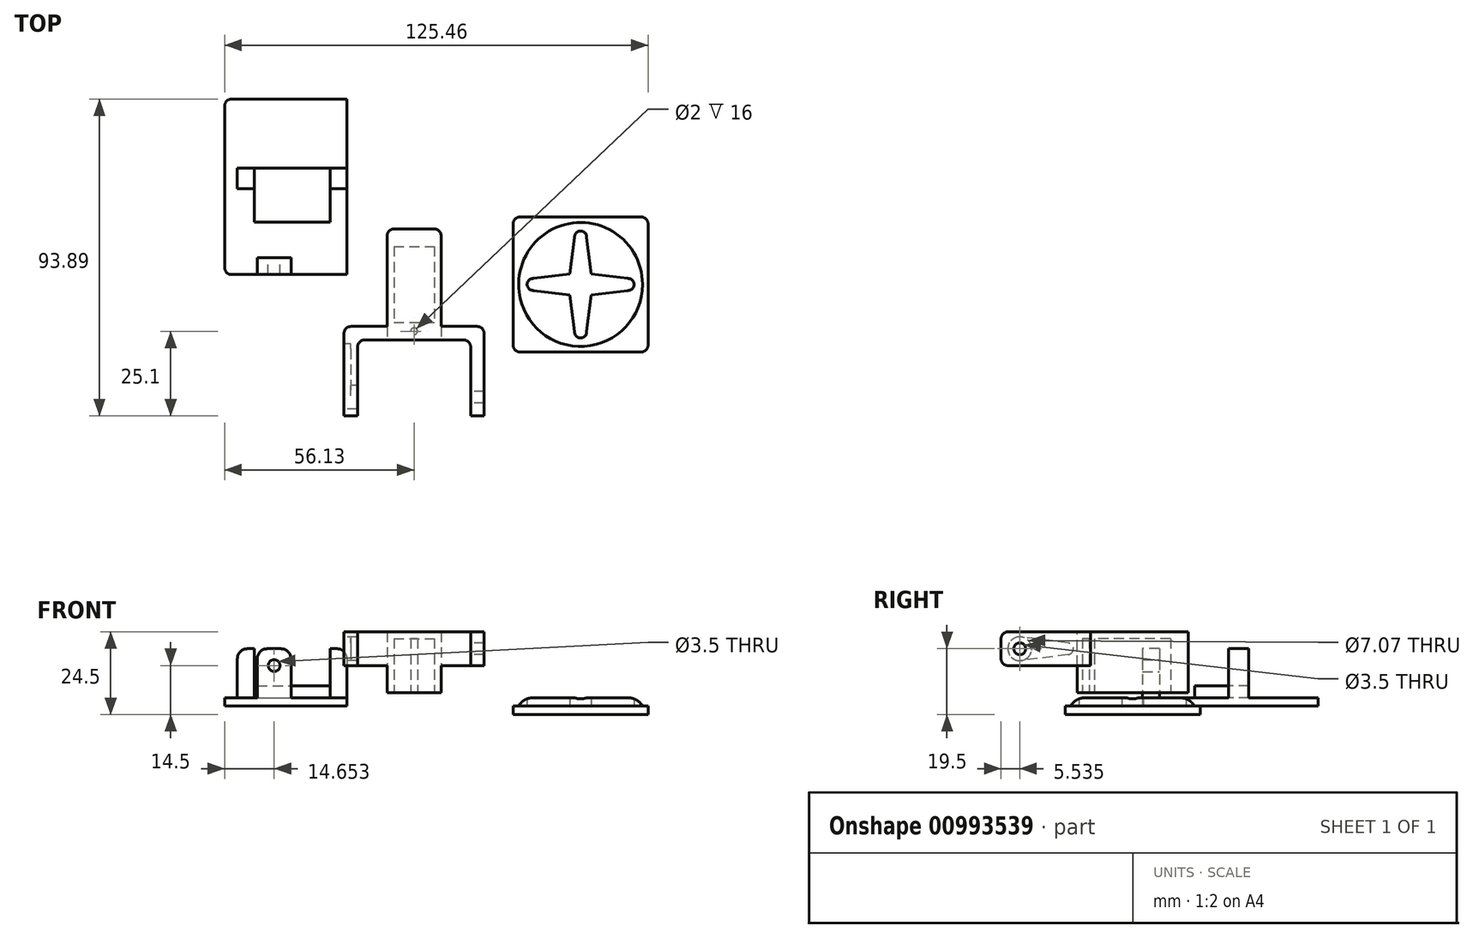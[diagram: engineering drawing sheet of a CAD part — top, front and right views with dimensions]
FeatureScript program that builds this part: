
annotation { "Feature Type Name" : "Feature", "Feature Type Description" : "" }
export const myFeature = defineFeature(function(context is Context, id is Id, definition is map)
    precondition{}
    {
        {
            var Q0;
            Q0=qCreatedBy(makeId("Top.planeOp"),FACE);
            var sketch = newSketch(context, id + "F0", { "sketchPlane" : qUnion([Q0])});
            skLineSegment(sketch, "E0.bottom", {"start": v(-6, 11.25) * mm, "end": v(6, 11.25) * mm});
            skLineSegment(sketch, "E0.top", {"start": v(-6, -11.25) * mm, "end": v(6, -11.25) * mm});
            skLineSegment(sketch, "E0.left", {"start": v(-6, 11.25) * mm, "end": v(-6, -11.25) * mm});
            skLineSegment(sketch, "E0.right", {"start": v(6, 11.25) * mm, "end": v(6, -11.25) * mm});
            skLineSegment(sketch, "E1.bottom", {"start": v(-8, 16.45) * mm, "end": v(8, 16.45) * mm});
            skLineSegment(sketch, "E1.top", {"start": v(-8, -16.45) * mm, "end": v(8, -16.45) * mm});
            skLineSegment(sketch, "E1.left", {"start": v(-8, 16.45) * mm, "end": v(-8, -16.45) * mm});
            skLineSegment(sketch, "E1.right", {"start": v(8, 16.45) * mm, "end": v(8, -16.45) * mm});
            skCircle(sketch, "E2", {"center": v(0, 13.85) * mm, "radius": 1 * mm});
            skLineSegment(sketch, "E3", {"start": v(-8, 0) * mm, "end": v(8, 0) * mm, "construction": true});
            skPoint(sketch, "E3.endSnap0", {"position": v(6, 0) * mm});
            skLineSegment(sketch, "E4", {"start": v(0, 13.85) * mm, "end": v(0, 13.85) * mm});
            skLineSegment(sketch, "E5", {"start": v(0, 0) * mm, "end": v(0, 13.85) * mm, "construction": true});
            skCircle(sketch, "E6.MirrorC", {"center": v(0, -13.85) * mm, "radius": 1 * mm});
            skLineSegment(sketch, "E7", {"start": v(0, -16.45) * mm, "end": v(0, -13.85) * mm, "construction": true});
            skLineSegment(sketch, "E8", {"start": v(0, -11.25) * mm, "end": v(0, -13.85) * mm, "construction": true});
            skSolve(sketch);
        }
        {
            var Q0;
            Q0=makeQuery(id+"F0.imprint","IMPRINT",FACE,{"disambiguationData":[TD([[makeQuery(id+"F0.imprint","IMPRINT",EDGE,{"derivedFrom":sQuery(id+"F0.wireOp",EDGE,"E2")}),1.0]])]});
            var Q1;
            Q1=makeQuery(id+"F0.imprint","IMPRINT",FACE,{"disambiguationData":[TD([[makeQuery(id+"F0.imprint","IMPRINT",EDGE,{"derivedFrom":sQuery(id+"F0.wireOp",EDGE,"E2")}),1.0]])]});
            var Q2;
            Q2=makeQuery(id+"F0.imprint","IMPRINT",FACE,{"disambiguationData":[TD([[makeQuery(id+"F0.imprint","IMPRINT",EDGE,{"derivedFrom":sQuery(id+"F0.wireOp",EDGE,"E6.MirrorC")}),-1.0]])]});
            var Q3;
            Q3=makeQuery(id+"F0.imprint","IMPRINT",FACE,{"disambiguationData":[TD([[makeQuery(id+"F0.imprint","IMPRINT",EDGE,{"derivedFrom":sQuery(id+"F0.wireOp",EDGE,"E0.bottom")}),1.0]])]});
            var Q4;
            Q4=makeQuery(id+"F0.imprint","IMPRINT",FACE,{"disambiguationData":[TD([[makeQuery(id+"F0.imprint","IMPRINT",EDGE,{"derivedFrom":sQuery(id+"F0.wireOp",EDGE,"E6.MirrorC")}),-1.0]])]});
            extrude(context, id + "F1", {"entities" : qUnion([Q0, Q1, Q2, Q3, Q4]), "depth" : 20 * mm, "offsetDistance" : 25 * mm});
        }
        {
            var Q0;
            Q0=makeQuery(id+"F0.imprint","IMPRINT",FACE,{"disambiguationData":[TD([[makeQuery(id+"F0.imprint","IMPRINT",EDGE,{"derivedFrom":sQuery(id+"F0.wireOp",EDGE,"E2")}),1.0]])]});
            var Q1;
            Q1=makeQuery(id+"F0.imprint","IMPRINT",FACE,{"disambiguationData":[TD([[makeQuery(id+"F0.imprint","IMPRINT",EDGE,{"derivedFrom":sQuery(id+"F0.wireOp",EDGE,"E2")}),1.0]])]});
            var Q2;
            Q2=makeQuery(id+"F0.imprint","IMPRINT",FACE,{"disambiguationData":[TD([[makeQuery(id+"F0.imprint","IMPRINT",EDGE,{"derivedFrom":sQuery(id+"F0.wireOp",EDGE,"E6.MirrorC")}),-1.0]])]});
            var Q3;
            Q3=makeQuery(id+"F0.imprint","IMPRINT",FACE,{"disambiguationData":[TD([[makeQuery(id+"F0.imprint","IMPRINT",EDGE,{"derivedFrom":sQuery(id+"F0.wireOp",EDGE,"E6.MirrorC")}),-1.0]])]});
            extrude(context, id + "F2", {"entities" : qUnion([Q0, Q1, Q2, Q3]), "operationType" : NewBodyOperationType.REMOVE, "depth" : 4 * mm, "offsetDistance" : 25 * mm});
        }
        {
            var Q0;
            Q0=makeQuery(id+"F1.opExtrude","CAP_FACE",FACE,{"disambiguationData":[OSD([sQuery(id+"F0.wireOp",EDGE,"E0.bottom"),sQuery(id+"F0.wireOp",EDGE,"E0.top"),sQuery(id+"F0.wireOp",EDGE,"E0.left"),sQuery(id+"F0.wireOp",EDGE,"E0.right"),sQuery(id+"F0.wireOp",EDGE,"E1.bottom"),sQuery(id+"F0.wireOp",EDGE,"E1.top"),sQuery(id+"F0.wireOp",EDGE,"E1.left"),sQuery(id+"F0.wireOp",EDGE,"E1.right")])],"isStart":false});
            var sketch = newSketch(context, id + "F3", { "sketchPlane" : qUnion([Q0])});
            skLineSegment(sketch, "E9.bottom", {"start": v(-8, 16.45) * mm, "end": v(8, 16.45) * mm});
            skLineSegment(sketch, "E9.top", {"start": v(-8, -16.45) * mm, "end": v(8, -16.45) * mm});
            skLineSegment(sketch, "E9.left", {"start": v(-8, 16.45) * mm, "end": v(-8, -16.45) * mm});
            skLineSegment(sketch, "E9.right", {"start": v(8, 16.45) * mm, "end": v(8, -16.45) * mm});
            skSolve(sketch);
        }
        {
            var Q0;
            Q0 = qSketchRegion(id + "F3", true);
            extrude(context, id + "F4", {"entities" : qUnion([Q0]), "operationType" : NewBodyOperationType.ADD, "depth" : 2 * mm, "offsetDistance" : 25 * mm});
        }
        {
            var Q0;
            Q0=makeQuery(id+"F4.opExtrude","CAP_FACE",FACE,{"disambiguationData":[OSD([sQuery(id+"F3.wireOp",EDGE,"E9.bottom"),sQuery(id+"F3.wireOp",EDGE,"E9.top"),sQuery(id+"F3.wireOp",EDGE,"E9.left"),sQuery(id+"F3.wireOp",EDGE,"E9.right")])],"isStart":false});
            var sketch = newSketch(context, id + "F5", { "sketchPlane" : qUnion([Q0])});
            skLineSegment(sketch, "E10", {"start": v(-16.75, -16.45) * mm, "end": v(16.75, -16.45) * mm});
            skLineSegment(sketch, "E11", {"start": v(-16.75, -16.45) * mm, "end": v(-16.75, -38.95) * mm});
            skLineSegment(sketch, "E12", {"start": v(-16.75, -38.95) * mm, "end": v(-20.75, -38.95) * mm});
            skLineSegment(sketch, "E13", {"start": v(-20.75, -38.95) * mm, "end": v(-20.75, -12.45) * mm});
            skLineSegment(sketch, "E14", {"start": v(-20.75, -12.45) * mm, "end": v(-8, -12.45) * mm});
            skLineSegment(sketch, "E15", {"start": v(16.75, -16.45) * mm, "end": v(16.75, -38.95) * mm});
            skLineSegment(sketch, "E16", {"start": v(16.75, -38.95) * mm, "end": v(20.75, -38.95) * mm});
            skLineSegment(sketch, "E17", {"start": v(20.75, -38.95) * mm, "end": v(20.75, -12.45) * mm});
            skLineSegment(sketch, "E18", {"start": v(20.75, -12.45) * mm, "end": v(8, -12.45) * mm});
            skLineSegment(sketch, "E19", {"start": v(16.75, -16.45) * mm, "end": v(20.75, -12.45) * mm, "construction": true});
            skSolve(sketch);
        }
        {
            var Q0;
            Q0 = qSketchRegion(id + "F5", true);
            var Q1;
            {var subQ0=sQuery(id+"F5.wireOp",EDGE,"E15");Q1=makeQuery(id+"F5.imprint","IMPRINT",FACE,{"disambiguationData":[TD([[makeQuery(id+"F5.imprint","IMPRINT",EDGE,{"derivedFrom":subQ0}),1.0]])]});}
            var Q2;
            {var subQ0=sQuery(id+"F5.wireOp",EDGE,"E11");Q2=makeQuery(id+"F5.imprint","IMPRINT",FACE,{"disambiguationData":[TD([[makeQuery(id+"F5.imprint","IMPRINT",EDGE,{"derivedFrom":subQ0}),-1.0]])]});}
            extrude(context, id + "F6", {"entities" : qUnion([Q0, Q1, Q2]), "operationType" : NewBodyOperationType.ADD, "oppositeDirection" : true, "depth" : 10 * mm, "offsetDistance" : 25 * mm});
        }
        {
            var Q0;
            Q0=makeQuery(id+"F6.opExtrude","SWEPT_EDGE",EDGE,{"disambiguationData":[OSD([sQuery(id+"F5.wireOp",EDGE,"E13"),sQuery(id+"F5.wireOp",EDGE,"E14")])]});
            var Q1;
            Q1=makeQuery(id+"F6.opExtrude","SWEPT_EDGE",EDGE,{"disambiguationData":[OSD([sQuery(id+"F5.wireOp",EDGE,"E17"),sQuery(id+"F5.wireOp",EDGE,"E18")])]});
            var Q2;
            Q2=makeQuery(id+"F6.opExtrude","CAP_EDGE",EDGE,{"disambiguationData":[OSD([sQuery(id+"F5.wireOp",EDGE,"E16")])],"isStart":true});
            var Q3;
            Q3=makeQuery(id+"F6.opExtrude","CAP_EDGE",EDGE,{"disambiguationData":[OSD([sQuery(id+"F5.wireOp",EDGE,"E16")])],"isStart":false});
            var Q4;
            Q4=makeQuery(id+"F6.opExtrude","CAP_EDGE",EDGE,{"disambiguationData":[OSD([sQuery(id+"F5.wireOp",EDGE,"E12")])],"isStart":true});
            var Q5;
            Q5=makeQuery(id+"F6.opExtrude","CAP_EDGE",EDGE,{"disambiguationData":[OSD([sQuery(id+"F5.wireOp",EDGE,"E12")])],"isStart":false});
            var Q6;
            Q6=makeQuery(id+"F6.opExtrude","SWEPT_EDGE",EDGE,{"disambiguationData":[OSD([sQuery(id+"F5.wireOp",EDGE,"E10"),sQuery(id+"F5.wireOp",EDGE,"E11")])]});
            var Q7;
            Q7=makeQuery(id+"F6.opExtrude","SWEPT_EDGE",EDGE,{"disambiguationData":[OSD([sQuery(id+"F5.wireOp",EDGE,"E10"),sQuery(id+"F5.wireOp",EDGE,"E15")])]});
            var Q8;
            Q8=makeQuery(id+"F4.boolean.opBoolean","MERGE",EDGE,{"derivedFrom":[makeQuery(id+"F1.opExtrude","SWEPT_EDGE",EDGE,{"disambiguationData":[OSD([sQuery(id+"F0.wireOp",EDGE,"E1.bottom"),sQuery(id+"F0.wireOp",EDGE,"E1.left")])]}),makeQuery(id+"F4.opExtrude","SWEPT_EDGE",EDGE,{"disambiguationData":[OSD([sQuery(id+"F3.wireOp",EDGE,"E9.bottom"),sQuery(id+"F3.wireOp",EDGE,"E9.left")])]})]});
            var Q9;
            Q9=makeQuery(id+"F4.boolean.opBoolean","MERGE",EDGE,{"derivedFrom":[makeQuery(id+"F1.opExtrude","SWEPT_EDGE",EDGE,{"disambiguationData":[OSD([sQuery(id+"F0.wireOp",EDGE,"E1.bottom"),sQuery(id+"F0.wireOp",EDGE,"E1.right")])]}),makeQuery(id+"F4.opExtrude","SWEPT_EDGE",EDGE,{"disambiguationData":[OSD([sQuery(id+"F3.wireOp",EDGE,"E9.bottom"),sQuery(id+"F3.wireOp",EDGE,"E9.right")])]})]});
            fillet(context, id + "F7", {"entities" : qUnion([Q0, Q1, Q2, Q3, Q4, Q5, Q6, Q7, Q8, Q9]), "radius" : 2 * mm, "tangentPropagation" : true, "allowEdgeOverflow" : false});
        }
        {
            var Q0;
            Q0=makeQuery(id+"F6.opExtrude","SWEPT_FACE",FACE,{"disambiguationData":[OSD([sQuery(id+"F5.wireOp",EDGE,"E13")])]});
            var sketch = newSketch(context, id + "F8", { "sketchPlane" : qUnion([Q0])});
            skCircle(sketch, "E20", {"center": v(33.41, 17) * mm, "radius": 3.54 * mm});
            skCircle(sketch, "E21", {"center": v(19.33, 17) * mm, "radius": 1.78 * mm});
            skLineSegment(sketch, "E22", {"start": v(14.45, 17) * mm, "end": v(38.95, 17) * mm, "construction": true});
            skLineSegment(sketch, "E23", {"start": v(19.1, 18.77) * mm, "end": v(32.97, 20.5) * mm});
            skLineSegment(sketch, "E24.MirrorCS", {"start": v(19.1, 15.23) * mm, "end": v(32.97, 13.5) * mm});
            skPoint(sketch, "E25", {"position": v(17.55, 17) * mm});
            skPoint(sketch, "E26", {"position": v(36.95, 17) * mm});
            skSolve(sketch);
        }
        {
            var Q0;
            {var subQ0=sQuery(id+"F8.wireOp",EDGE,"E21");var subQ1=makeQuery(id+"F8.imprint","INTERSECT",VERTEX,{"derivedFrom":[subQ0,sQuery(id+"F8.wireOp",EDGE,"E23")]});Q0=makeQuery(id+"F8.imprint","IMPRINT",FACE,{"disambiguationData":[TD([[makeQuery(id+"F8.imprint","IMPRINT",EDGE,{"disambiguationData":[TD([[subQ1,-1.0]])],"derivedFrom":subQ0}),1.0]])]});}
            var Q1;
            {var subQ0=sQuery(id+"F8.wireOp",EDGE,"E23");Q1=makeQuery(id+"F8.imprint","IMPRINT",FACE,{"disambiguationData":[TD([[makeQuery(id+"F8.imprint","IMPRINT",EDGE,{"derivedFrom":subQ0}),-1.0]])]});}
            var Q2;
            {var subQ0=sQuery(id+"F8.wireOp",EDGE,"E20");var subQ1=makeQuery(id+"F8.imprint","INTERSECT",VERTEX,{"derivedFrom":[subQ0,sQuery(id+"F8.wireOp",EDGE,"E23")]});Q2=makeQuery(id+"F8.imprint","IMPRINT",FACE,{"disambiguationData":[TD([[makeQuery(id+"F8.imprint","IMPRINT",EDGE,{"disambiguationData":[TD([[subQ1,-1.0]])],"derivedFrom":subQ0}),1.0]])]});}
            extrude(context, id + "F9", {"entities" : qUnion([Q0, Q1, Q2]), "operationType" : NewBodyOperationType.REMOVE, "oppositeDirection" : true, "depth" : 2 * mm, "offsetDistance" : 25 * mm});
        }
        {
            var Q0;
            {var subQ0=sQuery(id+"F8.wireOp",EDGE,"E20");var subQ1=makeQuery(id+"F8.imprint","INTERSECT",VERTEX,{"derivedFrom":[subQ0,sQuery(id+"F8.wireOp",EDGE,"E23")]});Q0=makeQuery(id+"F8.imprint","IMPRINT",FACE,{"disambiguationData":[TD([[makeQuery(id+"F8.imprint","IMPRINT",EDGE,{"disambiguationData":[TD([[subQ1,-1.0]])],"derivedFrom":subQ0}),1.0]])]});}
            var Q1;
            Q1=makeQuery(id+"F6.opExtrude","SWEPT_FACE",FACE,{"disambiguationData":[OSD([sQuery(id+"F5.wireOp",EDGE,"E11")])]});
            extrude(context, id + "F10", {"entities" : qUnion([Q0]), "operationType" : NewBodyOperationType.REMOVE, "endBound" : BoundingType.UP_TO_SURFACE, "oppositeDirection" : true, "depth" : 25 * mm, "endBoundEntityFace" : qUnion([Q1]), "offsetDistance" : 25 * mm});
        }
        {
            var Q0;
            Q0=qCreatedBy(makeId("Top.planeOp"),FACE);
            var sketch = newSketch(context, id + "F11", { "sketchPlane" : qUnion([Q0])});
            skLineSegment(sketch, "E27.bottom", {"start": v(-56.13, 42.94) * mm, "end": v(-16.13, 42.94) * mm});
            skLineSegment(sketch, "E27.top", {"start": v(-56.13, 2.94) * mm, "end": v(-16.13, 2.94) * mm});
            skLineSegment(sketch, "E27.left", {"start": v(-56.13, 42.94) * mm, "end": v(-56.13, 2.94) * mm});
            skLineSegment(sketch, "E27.right", {"start": v(-16.13, 42.94) * mm, "end": v(-16.13, 2.94) * mm});
            skSolve(sketch);
        }
        {
            var Q0;
            Q0=makeQuery(id+"F11.imprint","IMPRINT",FACE,{"disambiguationData":[TD([[makeQuery(id+"F11.imprint","IMPRINT",EDGE,{"derivedFrom":sQuery(id+"F11.wireOp",EDGE,"E27.bottom")}),-1.0]])]});
            extrude(context, id + "F12", {"entities" : qUnion([Q0]), "depth" : 2.5 * mm, "offsetDistance" : 25 * mm});
        }
        {
            var Q0;
            Q0=makeQuery(id+"F12.opExtrude","CAP_FACE",FACE,{"disambiguationData":[OSD([sQuery(id+"F11.wireOp",EDGE,"E27.bottom"),sQuery(id+"F11.wireOp",EDGE,"E27.top"),sQuery(id+"F11.wireOp",EDGE,"E27.left"),sQuery(id+"F11.wireOp",EDGE,"E27.right")])],"isStart":false});
            var sketch = newSketch(context, id + "F13", { "sketchPlane" : qUnion([Q0])});
            skLineSegment(sketch, "E28.bottom", {"start": v(-47.38, 34.44) * mm, "end": v(-24.88, 34.44) * mm});
            skLineSegment(sketch, "E28.top", {"start": v(-47.38, 18.44) * mm, "end": v(-24.88, 18.44) * mm});
            skLineSegment(sketch, "E28.left", {"start": v(-47.38, 34.44) * mm, "end": v(-47.38, 18.44) * mm});
            skLineSegment(sketch, "E28.right", {"start": v(-24.88, 34.44) * mm, "end": v(-24.88, 18.44) * mm});
            skPoint(sketch, "E29", {"position": v(-36.13, 26.44) * mm});
            skLineSegment(sketch, "E30.bottom", {"start": v(-24.88, 34.44) * mm, "end": v(-19.88, 34.44) * mm});
            skLineSegment(sketch, "E30.top", {"start": v(-24.88, 28.44) * mm, "end": v(-19.88, 28.44) * mm});
            skLineSegment(sketch, "E30.left", {"start": v(-24.88, 34.44) * mm, "end": v(-24.88, 28.44) * mm});
            skLineSegment(sketch, "E30.right", {"start": v(-19.88, 34.44) * mm, "end": v(-19.88, 28.44) * mm});
            skLineSegment(sketch, "E31.bottom", {"start": v(-47.38, 34.44) * mm, "end": v(-52.38, 34.44) * mm});
            skLineSegment(sketch, "E31.top", {"start": v(-47.38, 28.44) * mm, "end": v(-52.38, 28.44) * mm});
            skLineSegment(sketch, "E31.left", {"start": v(-47.38, 34.44) * mm, "end": v(-47.38, 28.44) * mm});
            skLineSegment(sketch, "E31.right", {"start": v(-52.38, 34.44) * mm, "end": v(-52.38, 28.44) * mm});
            skLineSegment(sketch, "E32", {"start": v(-41.48, 2.94) * mm, "end": v(-41.48, 42.94) * mm, "construction": true});
            skLineSegment(sketch, "E33.bottom", {"start": v(-46.48, 7.94) * mm, "end": v(-36.48, 7.94) * mm});
            skLineSegment(sketch, "E33.top", {"start": v(-46.48, 2.94) * mm, "end": v(-36.48, 2.94) * mm});
            skLineSegment(sketch, "E33.left", {"start": v(-46.48, 7.94) * mm, "end": v(-46.48, 2.94) * mm});
            skLineSegment(sketch, "E33.right", {"start": v(-36.48, 7.94) * mm, "end": v(-36.48, 2.94) * mm});
            skSolve(sketch);
        }
        {
            var Q0;
            {var subQ0=sQuery(id+"F13.wireOp",EDGE,"E31.bottom");Q0=makeQuery(id+"F13.imprint","IMPRINT",FACE,{"disambiguationData":[TD([[makeQuery(id+"F13.imprint","IMPRINT",EDGE,{"derivedFrom":subQ0}),1.0]])]});}
            var Q1;
            {var subQ0=sQuery(id+"F13.wireOp",EDGE,"E30.bottom");Q1=makeQuery(id+"F13.imprint","IMPRINT",FACE,{"disambiguationData":[TD([[makeQuery(id+"F13.imprint","IMPRINT",EDGE,{"derivedFrom":subQ0}),-1.0]])]});}
            var Q2;
            Q2=makeQuery(id+"F13.imprint","IMPRINT",FACE,{"disambiguationData":[TD([[makeQuery(id+"F13.imprint","IMPRINT",EDGE,{"derivedFrom":sQuery(id+"F13.wireOp",EDGE,"E33.bottom")}),-1.0]])]});
            extrude(context, id + "F14", {"entities" : qUnion([Q0, Q1, Q2]), "operationType" : NewBodyOperationType.ADD, "depth" : 14.5 * mm, "offsetDistance" : 25 * mm});
        }
        {
            var Q0;
            {var subQ1=sQuery(id+"F13.wireOp",EDGE,"E28.bottom");Q0=makeQuery(id+"F13.imprint","IMPRINT",FACE,{"disambiguationData":[TD([[makeQuery(id+"F13.imprint","IMPRINT",EDGE,{"derivedFrom":subQ1}),-1.0]])]});}
            extrude(context, id + "F15", {"entities" : qUnion([Q0]), "operationType" : NewBodyOperationType.ADD, "depth" : 3.5 * mm, "offsetDistance" : 25 * mm});
        }
        {
            var Q0;
            Q0=makeQuery(id+"F14.opExtrude","CAP_EDGE",EDGE,{"disambiguationData":[OSD([sQuery(id+"F13.wireOp",EDGE,"E31.right")])],"isStart":false});
            var Q1;
            Q1=makeQuery(id+"F14.opExtrude","CAP_EDGE",EDGE,{"disambiguationData":[OSD([sQuery(id+"F13.wireOp",EDGE,"E30.right")])],"isStart":false});
            var Q2;
            Q2=makeQuery(id+"F14.opExtrude","CAP_EDGE",EDGE,{"disambiguationData":[OSD([sQuery(id+"F13.wireOp",EDGE,"E33.left")])],"isStart":false});
            var Q3;
            Q3=makeQuery(id+"F14.opExtrude","CAP_EDGE",EDGE,{"disambiguationData":[OSD([sQuery(id+"F13.wireOp",EDGE,"E33.right")])],"isStart":false});
            fillet(context, id + "F16", {"entities" : qUnion([Q0, Q1, Q2, Q3]), "radius" : 3 * mm, "allowEdgeOverflow" : false});
        }
        {
            var Q0;
            Q0=makeQuery(id+"F12.opExtrude","SWEPT_FACE",FACE,{"disambiguationData":[OSD([sQuery(id+"F11.wireOp",EDGE,"E27.bottom")])]});
            extrude(context, id + "F17", {"entities" : qUnion([Q0]), "operationType" : NewBodyOperationType.ADD, "depth" : 12 * mm, "offsetDistance" : 25 * mm});
        }
        {
            var Q0;
            {var subQ0=sQuery(id+"F11.wireOp",EDGE,"E27.right");Q0=makeQuery(id+"F17.boolean.opBoolean","MERGE",FACE,{"derivedFrom":[makeQuery(id+"F12.opExtrude","SWEPT_FACE",FACE,{"disambiguationData":[OSD([subQ0])]}),makeQuery(id+"F17.opExtrude","SWEPT_FACE",FACE,{"disambiguationData":[OSD([sQuery(id+"F11.wireOp",EDGE,"E27.bottom"),subQ0])]})]});}
            var Q1;
            Q1=makeQuery(id+"F14.opExtrude","SWEPT_FACE",FACE,{"disambiguationData":[OSD([sQuery(id+"F13.wireOp",EDGE,"E30.right")])]});
            extrude(context, id + "F18", {"entities" : qUnion([Q0]), "operationType" : NewBodyOperationType.REMOVE, "endBound" : BoundingType.UP_TO_SURFACE, "oppositeDirection" : true, "depth" : 25 * mm, "endBoundEntityFace" : qUnion([Q1]), "offsetDistance" : 25 * mm});
        }
        {
            var Q0;
            Q0=makeQuery(id+"F6.opExtrude","SWEPT_FACE",FACE,{"disambiguationData":[OSD([sQuery(id+"F5.wireOp",EDGE,"E15")])]});
            var sketch = newSketch(context, id + "F19", { "sketchPlane" : qUnion([Q0])});
            skCircle(sketch, "E34", {"center": v(33.41, 17) * mm, "radius": 1.75 * mm});
            skSolve(sketch);
        }
        {
            var Q0;
            Q0=makeQuery(id+"F19.imprint","IMPRINT",FACE,{"disambiguationData":[TD([[makeQuery(id+"F19.imprint","IMPRINT",EDGE,{"derivedFrom":sQuery(id+"F19.wireOp",EDGE,"E34")}),1.0]])]});
            var Q1;
            Q1=makeQuery(id+"F6.opExtrude","SWEPT_FACE",FACE,{"disambiguationData":[OSD([sQuery(id+"F5.wireOp",EDGE,"E17")])]});
            extrude(context, id + "F20", {"entities" : qUnion([Q0]), "operationType" : NewBodyOperationType.REMOVE, "endBound" : BoundingType.UP_TO_SURFACE, "oppositeDirection" : true, "depth" : 25 * mm, "endBoundEntityFace" : qUnion([Q1]), "offsetDistance" : 25 * mm});
        }
        {
            var Q0;
            Q0=makeQuery(id+"F14.opExtrude","SWEPT_FACE",FACE,{"disambiguationData":[OSD([sQuery(id+"F13.wireOp",EDGE,"E33.bottom")])]});
            var sketch = newSketch(context, id + "F21", { "sketchPlane" : qUnion([Q0])});
            skCircle(sketch, "E35", {"center": v(41.48, 12) * mm, "radius": 1.75 * mm});
            skSolve(sketch);
        }
        {
            var Q0;
            Q0=makeQuery(id+"F21.imprint","IMPRINT",FACE,{"disambiguationData":[TD([[makeQuery(id+"F21.imprint","IMPRINT",EDGE,{"derivedFrom":sQuery(id+"F21.wireOp",EDGE,"E35")}),1.0]])]});
            var Q1;
            Q1=makeQuery(id+"F14.boolean.opBoolean","MERGE",FACE,{"derivedFrom":[makeQuery(id+"F12.opExtrude","SWEPT_FACE",FACE,{"disambiguationData":[OSD([sQuery(id+"F11.wireOp",EDGE,"E27.top")])]}),makeQuery(id+"F14.opExtrude","SWEPT_FACE",FACE,{"disambiguationData":[OSD([sQuery(id+"F13.wireOp",EDGE,"E33.top")])]})]});
            extrude(context, id + "F22", {"entities" : qUnion([Q0]), "operationType" : NewBodyOperationType.REMOVE, "endBound" : BoundingType.UP_TO_SURFACE, "oppositeDirection" : true, "depth" : 25 * mm, "endBoundEntityFace" : qUnion([Q1]), "offsetDistance" : 25 * mm});
        }
        {
            var Q0;
            Q0=qCreatedBy(makeId("Top.planeOp"),FACE);
            var sketch = newSketch(context, id + "F23", { "sketchPlane" : qUnion([Q0])});
            skLineSegment(sketch, "E36.bottom", {"start": v(29.33, -20) * mm, "end": v(69.33, -20) * mm});
            skLineSegment(sketch, "E36.top", {"start": v(29.33, 20) * mm, "end": v(69.33, 20) * mm});
            skLineSegment(sketch, "E36.left", {"start": v(29.33, -20) * mm, "end": v(29.33, 20) * mm});
            skLineSegment(sketch, "E36.right", {"start": v(69.33, -20) * mm, "end": v(69.33, 20) * mm});
            skCircle(sketch, "E37", {"center": v(49.33, 0) * mm, "radius": 3.54 * mm, "construction": true});
            skCircle(sketch, "E38", {"center": v(35.24, 0) * mm, "radius": 1.78 * mm});
            skPoint(sketch, "E39", {"position": v(33.46, 0) * mm});
            skPoint(sketch, "E40", {"position": v(52.86, 0) * mm});
            skPoint(sketch, "E41", {"position": v(49.33, 20) * mm});
            skPoint(sketch, "E42", {"position": v(29.33, 0) * mm});
            skLineSegment(sketch, "E43", {"start": v(35.02, 1.77) * mm, "end": v(48.89, 3.5) * mm});
            skLineSegment(sketch, "E44", {"start": v(35.02, -1.77) * mm, "end": v(48.89, -3.5) * mm});
            skLineSegment(sketch, "E45.1.0", {"start": v(47.56, -14.3) * mm, "end": v(45.82, -0.44) * mm});
            skCircle(sketch, "E45.1.1", {"center": v(49.33, -14.09) * mm, "radius": 1.78 * mm});
            skLineSegment(sketch, "E45.1.2", {"start": v(51.1, -14.3) * mm, "end": v(52.84, -0.44) * mm});
            skLineSegment(sketch, "E45.2.0", {"start": v(63.64, -1.77) * mm, "end": v(49.77, -3.5) * mm});
            skCircle(sketch, "E45.2.1", {"center": v(63.41, 0) * mm, "radius": 1.78 * mm});
            skLineSegment(sketch, "E45.2.2", {"start": v(63.64, 1.77) * mm, "end": v(49.77, 3.5) * mm});
            skLineSegment(sketch, "E45.3.0", {"start": v(51.1, 14.3) * mm, "end": v(52.84, 0.44) * mm});
            skCircle(sketch, "E45.3.1", {"center": v(49.33, 14.09) * mm, "radius": 1.78 * mm});
            skLineSegment(sketch, "E45.3.2", {"start": v(47.56, 14.3) * mm, "end": v(45.82, 0.44) * mm});
            skSolve(sketch);
        }
        {
            var Q0;
            Q0=makeQuery(id+"F23.imprint","IMPRINT",FACE,{"disambiguationData":[TD([[makeQuery(id+"F23.imprint","IMPRINT",EDGE,{"derivedFrom":sQuery(id+"F23.wireOp",EDGE,"E36.bottom")}),1.0]])]});
            var Q1;
            {var subQ15=sQuery(id+"F23.wireOp",EDGE,"E43");var subQ16=sQuery(id+"F23.wireOp",EDGE,"E38");var subQ17=makeQuery(id+"F23.imprint","INTERSECT",VERTEX,{"derivedFrom":[subQ16,subQ15]});Q1=makeQuery(id+"F23.imprint","IMPRINT",FACE,{"disambiguationData":[TD([[makeQuery(id+"F23.imprint","IMPRINT",EDGE,{"disambiguationData":[TD([[subQ17,1.0]])],"derivedFrom":subQ16}),-1.0]])]});}
            var Q2;
            {var subQ0=sQuery(id+"F23.wireOp",EDGE,"E45.3.1");var subQ1=makeQuery(id+"F23.imprint","INTERSECT",VERTEX,{"derivedFrom":[sQuery(id+"F23.wireOp",EDGE,"E45.3.0"),subQ0]});Q2=makeQuery(id+"F23.imprint","IMPRINT",FACE,{"disambiguationData":[TD([[makeQuery(id+"F23.imprint","IMPRINT",EDGE,{"disambiguationData":[TD([[subQ1,-1.0]])],"derivedFrom":subQ0}),1.0]])]});}
            var Q3;
            {var subQ0=sQuery(id+"F23.wireOp",EDGE,"E38");var subQ1=makeQuery(id+"F23.imprint","INTERSECT",VERTEX,{"derivedFrom":[subQ0,sQuery(id+"F23.wireOp",EDGE,"E43")]});Q3=makeQuery(id+"F23.imprint","IMPRINT",FACE,{"disambiguationData":[TD([[makeQuery(id+"F23.imprint","IMPRINT",EDGE,{"disambiguationData":[TD([[subQ1,-1.0]])],"derivedFrom":subQ0}),1.0]])]});}
            var Q4;
            {var subQ0=sQuery(id+"F23.wireOp",EDGE,"E45.1.1");var subQ1=makeQuery(id+"F23.imprint","INTERSECT",VERTEX,{"derivedFrom":[sQuery(id+"F23.wireOp",EDGE,"E45.1.0"),subQ0]});Q4=makeQuery(id+"F23.imprint","IMPRINT",FACE,{"disambiguationData":[TD([[makeQuery(id+"F23.imprint","IMPRINT",EDGE,{"disambiguationData":[TD([[subQ1,-1.0]])],"derivedFrom":subQ0}),1.0]])]});}
            var Q5;
            {var subQ0=sQuery(id+"F23.wireOp",EDGE,"E45.2.1");var subQ1=makeQuery(id+"F23.imprint","INTERSECT",VERTEX,{"derivedFrom":[sQuery(id+"F23.wireOp",EDGE,"E45.2.0"),subQ0]});Q5=makeQuery(id+"F23.imprint","IMPRINT",FACE,{"disambiguationData":[TD([[makeQuery(id+"F23.imprint","IMPRINT",EDGE,{"disambiguationData":[TD([[subQ1,-1.0]])],"derivedFrom":subQ0}),1.0]])]});}
            extrude(context, id + "F24", {"entities" : qUnion([Q0, Q1, Q2, Q3, Q4, Q5]), "oppositeDirection" : true, "depth" : 2.5 * mm, "offsetDistance" : 25 * mm});
        }
        {
            var Q0;
            Q0=makeQuery(id+"F23.imprint","IMPRINT",FACE,{"disambiguationData":[TD([[makeQuery(id+"F23.imprint","IMPRINT",EDGE,{"derivedFrom":sQuery(id+"F23.wireOp",EDGE,"E36.bottom")}),1.0]])]});
            var sketch = newSketch(context, id + "F25", { "sketchPlane" : qUnion([Q0])});
            skCircle(sketch, "E46", {"center": v(49.33, 0) * mm, "radius": 18.37 * mm});
            skSolve(sketch);
        }
        {
            var Q0;
            Q0=makeQuery(id+"F25.imprint","IMPRINT",FACE,{"disambiguationData":[TD([[makeQuery(id+"F25.imprint","IMPRINT",EDGE,{"derivedFrom":sQuery(id+"F25.wireOp",EDGE,"E46")}),1.0]])]});
            extrude(context, id + "F26", {"entities" : qUnion([Q0]), "operationType" : NewBodyOperationType.ADD, "depth" : 2.5 * mm, "offsetDistance" : 25 * mm});
        }
        {
            var Q0;
            Q0=makeQuery(id+"F26.opExtrude","CAP_EDGE",EDGE,{"disambiguationData":[OSD([sQuery(id+"F25.wireOp",EDGE,"E46")])],"isStart":false});
            fillet(context, id + "F27", {"entities" : qUnion([Q0]), "radius" : 5 * mm, "tangentPropagation" : true, "allowEdgeOverflow" : false});
        }
        {
            var Q0;
            Q0=makeQuery(id+"F24.opExtrude","SWEPT_EDGE",EDGE,{"disambiguationData":[OSD([sQuery(id+"F23.wireOp",EDGE,"E36.top"),sQuery(id+"F23.wireOp",EDGE,"E36.left")])]});
            var Q1;
            Q1=makeQuery(id+"F24.opExtrude","SWEPT_EDGE",EDGE,{"disambiguationData":[OSD([sQuery(id+"F23.wireOp",EDGE,"E36.top"),sQuery(id+"F23.wireOp",EDGE,"E36.right")])]});
            var Q2;
            Q2=makeQuery(id+"F24.opExtrude","SWEPT_EDGE",EDGE,{"disambiguationData":[OSD([sQuery(id+"F23.wireOp",EDGE,"E36.bottom"),sQuery(id+"F23.wireOp",EDGE,"E36.right")])]});
            var Q3;
            Q3=makeQuery(id+"F24.opExtrude","SWEPT_EDGE",EDGE,{"disambiguationData":[OSD([sQuery(id+"F23.wireOp",EDGE,"E36.bottom"),sQuery(id+"F23.wireOp",EDGE,"E36.left")])]});
            fillet(context, id + "F28", {"entities" : qUnion([Q0, Q1, Q2, Q3]), "radius" : 2 * mm, "tangentPropagation" : true, "allowEdgeOverflow" : false});
        }
        {
            var Q0;
            Q0=makeQuery(id+"F12.opExtrude","SWEPT_EDGE",EDGE,{"disambiguationData":[OSD([sQuery(id+"F11.wireOp",EDGE,"E27.top"),sQuery(id+"F11.wireOp",EDGE,"E27.left")])]});
            var Q1;
            Q1=makeQuery(id+"F18.boolean.opBoolean","COPY",EDGE,{"derivedFrom":makeQuery(id+"F18.opExtrude","CAP_EDGE",EDGE,{"disambiguationData":[OSD([sQuery(id+"F11.wireOp",EDGE,"E27.top"),sQuery(id+"F11.wireOp",EDGE,"E27.right")])],"isStart":false})});
            var Q2;
            {var subQ0=sQuery(id+"F11.wireOp",EDGE,"E27.right");var subQ1=sQuery(id+"F11.wireOp",EDGE,"E27.bottom");Q2=makeQuery(id+"F18.boolean.opBoolean","COPY",EDGE,{"derivedFrom":makeQuery(id+"F18.opExtrude","CAP_EDGE",EDGE,{"disambiguationData":[OSD([subQ1,subQ0]),TDD([makeQuery(id+"F17.opExtrude","CAP_EDGE",EDGE,{"disambiguationData":[OSD([subQ1,subQ0])],"isStart":false})])],"isStart":false})});}
            var Q3;
            Q3=makeQuery(id+"F17.opExtrude","CAP_EDGE",EDGE,{"disambiguationData":[OSD([sQuery(id+"F11.wireOp",EDGE,"E27.bottom"),sQuery(id+"F11.wireOp",EDGE,"E27.left")])],"isStart":false});
            fillet(context, id + "F29", {"entities" : qUnion([Q0, Q1, Q2, Q3]), "radius" : 2 * mm, "tangentPropagation" : true, "allowEdgeOverflow" : false});
        }
    });
